# Revit family: LSTH
name_source: partatom
category: Lighting Fixtures
units: mm (PartAtom-declared; Revit-internal decimal feet)

## family parameters
Always vertical = Yes
Cut with Voids When Loaded = No
Host = Ceiling
Light Source = Yes
OmniClass Number = 23.80.70.11.14.17
OmniClass Title = Direct/Indirect
Part Type = Normal
Room Calculation Point = No
Round Connector Dimension = Use Diameter
Shared = No

## types (4) — shared parameters
Assembly Code = D5020200
Color Filter = 16777215
Description = LED Surface  Type H
Dimming Lamp Color Temperature Shift = <None>
Emit Shape Visible in Rendering = No
Housing Finish = Metal - Viscor - White
Lamp = LED
Lens Finish = Acrylic - Viscor - Frosted White Impact Resistant
Manufacturer = VISIONEERING by VISCOR
Model = LSTH
Tilt Angle = 90.00°
URL = https://www.viscor.com
Voltage = 120 V

## per-type parameters (varying)
| type | Apparent Load | Emit from Rectangle Length | Emit from Rectangle Width | Lamp Wattage | Length | Photometric Web File | Reflector Width | Width |
| LSTH2X2-LED840K020LUNV | 14 VA | 1' - 11 3/4" | 1' - 11 3/4" | 14 VA | 1' - 11 3/4" | LSTH2X2-LED840K020LUNV.ies | 0' - 11 7/8" | 1' - 11 3/4" |
| LSTH1x4-LED840K040LUNV | 33 VA | 3' - 11 3/4" | 0' - 11 3/4" | 33 VA | 3' - 11 3/4" | LSTH1x4-LED840K040LUNV.IES | 0' - 5 7/8" | 0' - 11 3/4" |
| LSTH2x4-LED840K040LUNV | 30 VA | 3' - 11 3/4" | 1' - 11 3/4" | 30 VA | 3' - 11 3/4" | LSTH2x4-LED840K040LUNV.IES | 0' - 11 7/8" | 1' - 11 3/4" |
| LSTH2X2-LED840K032LUNV | 23 VA | 1' - 11 3/4" | 1' - 11 3/4" | 23 VA | 1' - 11 3/4" | LSTH2X2-LED840K032LUNV.ies | 0' - 11 7/8" | 1' - 11 3/4" |

## geometry (parser evidence)
native form markers: Sweep x4
no freeform markers — native parametric forms only
